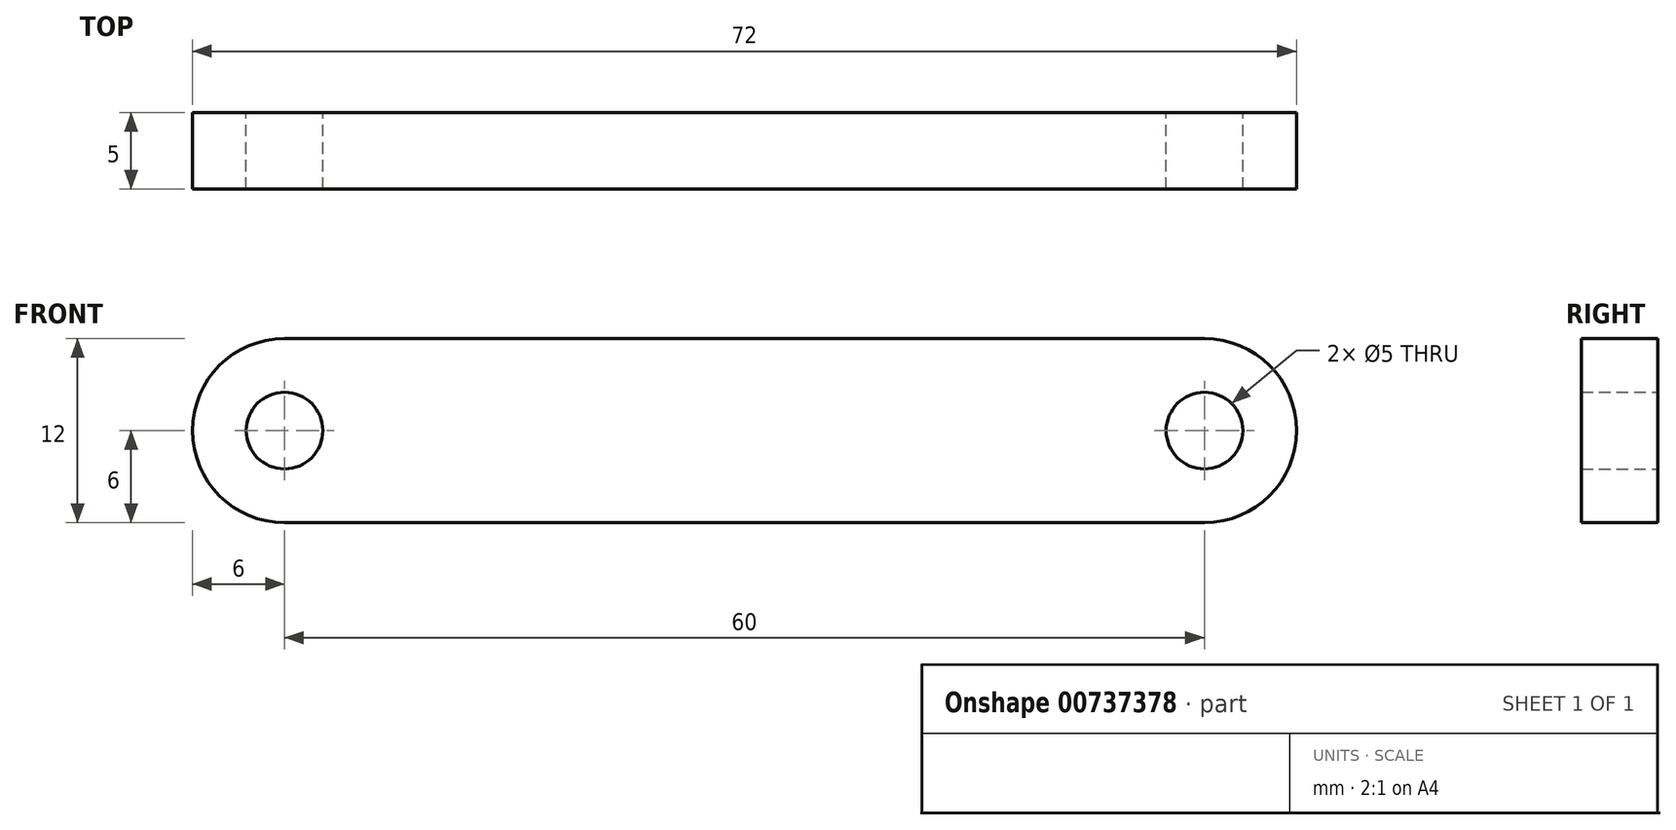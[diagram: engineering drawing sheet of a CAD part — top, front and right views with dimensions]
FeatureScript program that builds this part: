
annotation { "Feature Type Name" : "Feature", "Feature Type Description" : "" }
export const myFeature = defineFeature(function(context is Context, id is Id, definition is map)
    precondition{}
    {
        {
            var Q0;
            Q0=qCreatedBy(makeId("Front.planeOp"),FACE);
            var sketch = newSketch(context, id + "F0", { "sketchPlane" : qUnion([Q0])});
            skLineSegment(sketch, "E0.bottom", {"start": v(0, 0) * mm, "end": v(60, 0) * mm});
            skLineSegment(sketch, "E0.top", {"start": v(0, 12) * mm, "end": v(60, 12) * mm});
            skArc(sketch, "E1", {"start": v(60, 0) * mm, "mid": v(66, 6) * mm, "end": v(60, 12) * mm});
            skArc(sketch, "E2", {"start": v(0, 12) * mm, "mid": v(-6, 6) * mm, "end": v(0, 0) * mm});
            skCircle(sketch, "E3", {"center": v(0, 6) * mm, "radius": 2.5 * mm});
            skCircle(sketch, "E4", {"center": v(60, 6) * mm, "radius": 2.5 * mm});
            skSolve(sketch);
        }
        {
            var Q0;
            Q0=makeQuery(id+"F0.imprint","IMPRINT",FACE,{"disambiguationData":[TD([[makeQuery(id+"F0.imprint","IMPRINT",EDGE,{"derivedFrom":sQuery(id+"F0.wireOp",EDGE,"E0.bottom")}),1.0]])]});
            var Q1;
            Q1=makeQuery(id+"F0.imprint","IMPRINT",FACE,{"disambiguationData":[TD([[makeQuery(id+"F0.imprint","IMPRINT",EDGE,{"derivedFrom":sQuery(id+"F0.wireOp",EDGE,"i1ueIBZ2-LBOK-ZiPW-8Dnt-5YwOhWg0EiJV")}),1.0]])]});
            var Q2;
            Q2=makeQuery(id+"F0.imprint","IMPRINT",FACE,{"disambiguationData":[TD([[makeQuery(id+"F0.imprint","IMPRINT",EDGE,{"derivedFrom":sQuery(id+"F0.wireOp",EDGE,"1IPOGQ9F-0NTp-rzeO-0T4L-GCktHTDaA0Ut")}),1.0]])]});
            extrude(context, id + "F1", {"entities" : qUnion([Q0, Q1, Q2]), "depth" : 5 * mm, "offsetDistance" : 25 * mm});
        }
    });
